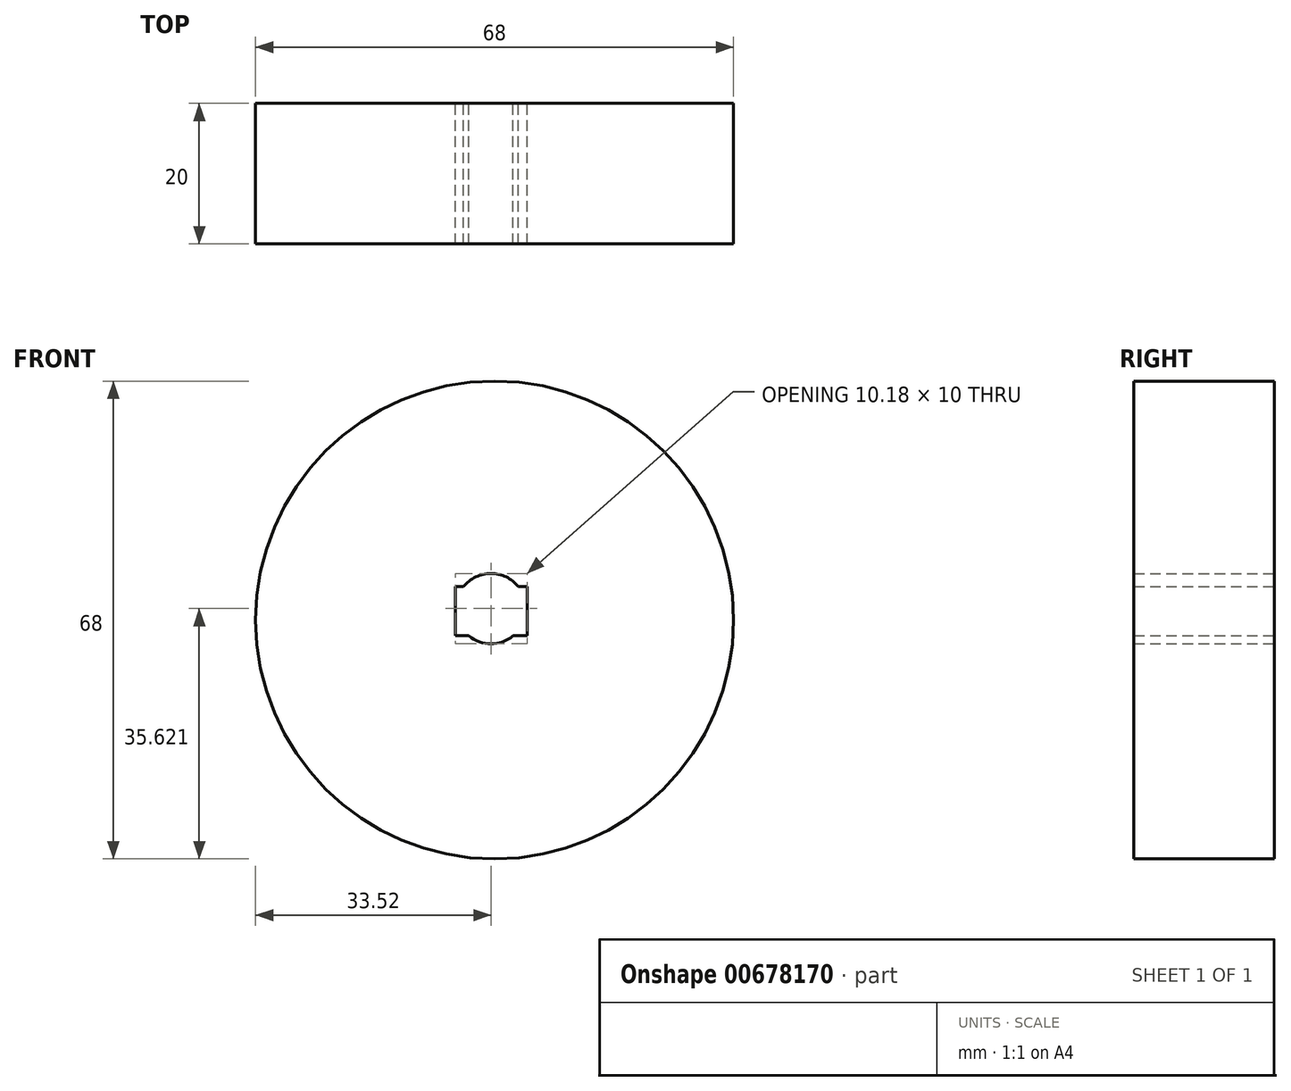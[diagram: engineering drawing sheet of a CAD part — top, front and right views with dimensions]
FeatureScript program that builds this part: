
annotation { "Feature Type Name" : "Feature", "Feature Type Description" : "" }
export const myFeature = defineFeature(function(context is Context, id is Id, definition is map)
    precondition{}
    {
        {
            var Q0;
            Q0=qCreatedBy(makeId("Front.planeOp"),FACE);
            var sketch = newSketch(context, id + "F0", { "sketchPlane" : qUnion([Q0])});
            skCircle(sketch, "E0", {"center": v(26.7, 8) * mm, "radius": 34 * mm});
            skSolve(sketch);
        }
        {
            var Q0;
            Q0=qSketchRegion(id+"F0",true);
            extrude(context, id + "F1", {"entities" : qUnion([Q0]), "depth" : 20 * mm, "offsetDistance" : 25 * mm});
        }
        {
            var Q0;
            Q0=qCreatedBy(makeId("Front.planeOp"),FACE);
            var sketch = newSketch(context, id + "F2", { "sketchPlane" : qUnion([Q0])});
            skCircle(sketch, "E1", {"center": v(26.17, 9.62) * mm, "radius": 5 * mm});
            skLineSegment(sketch, "E2.bottom", {"start": v(31.3, 5.74) * mm, "end": v(21.12, 5.74) * mm});
            skLineSegment(sketch, "E2.top", {"start": v(31.3, 12.74) * mm, "end": v(21.12, 12.74) * mm});
            skLineSegment(sketch, "E2.left", {"start": v(31.3, 5.74) * mm, "end": v(31.3, 12.74) * mm});
            skLineSegment(sketch, "E2.right", {"start": v(21.12, 5.74) * mm, "end": v(21.12, 12.74) * mm});
            skSolve(sketch);
        }
        {
            var Q0;
            Q0=qSketchRegion(id+"F2",true);
            extrude(context, id + "F3", {"entities" : qUnion([Q0]), "operationType" : NewBodyOperationType.REMOVE, "depth" : 69.9 * mm, "offsetDistance" : 25 * mm});
        }
    });
